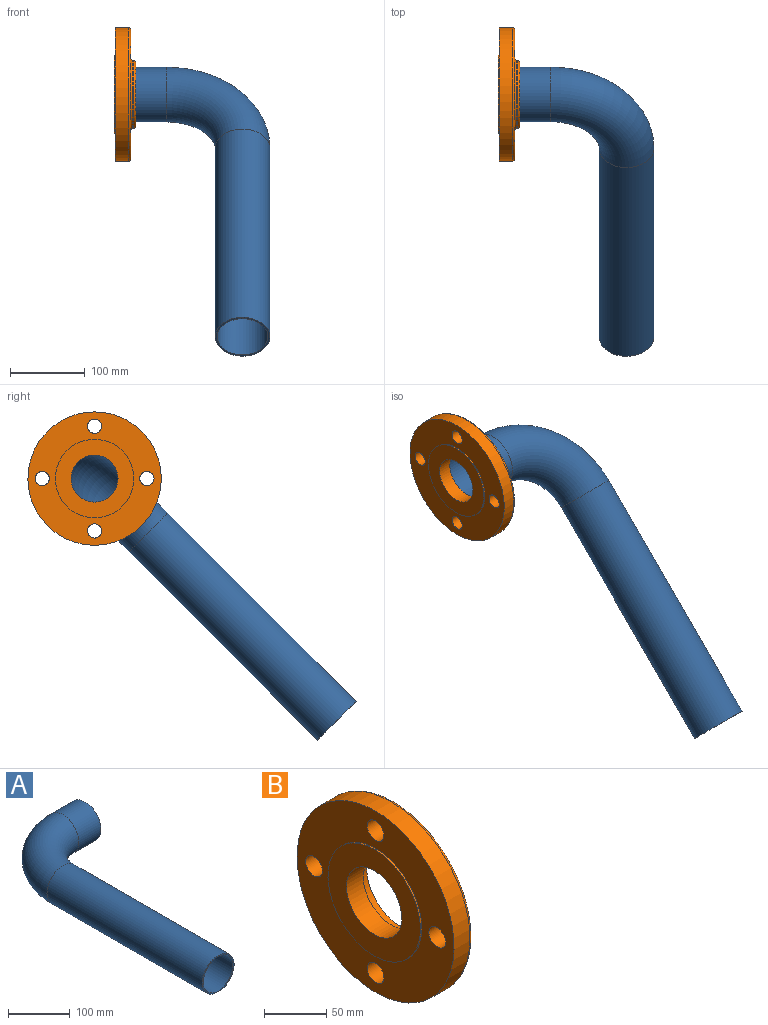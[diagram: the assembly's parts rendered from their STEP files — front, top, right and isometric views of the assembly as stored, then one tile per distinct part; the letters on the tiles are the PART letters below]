
ASSEMBLY  parts=2 mates=1
PART A: 8 faces, bbox 200.3x505.1x73 mm
  f0: plane 73.03x73.03mm, normal (0,-1,0), area 562.4mm2, adj f2,f5
  f1: plane 73.03x73.03mm, normal (1,0,0), area 562.4mm2, adj f4,f7
  f2: cylinder r=36.51mm len=355.6mm, axis (0,1,0), area 81579.9mm2, adj f0,f3
  f3: torus R=101.6mm, axis (0,0,-1), area 36613mm2, adj f2,f4
  f4: cylinder r=36.51mm len=73.03mm, axis (1,0,0), area 11654.3mm2, adj f1,f3
  f5: cylinder r=33.97mm len=355.6mm, axis (0,1,0), area 75904.8mm2, adj f0,f6
  f6: torus R=101.6mm, axis (0,0,-1), area 34066mm2, adj f5,f7
  f7: cylinder r=33.97mm len=67.95mm, axis (1,0,0), area 10843.5mm2, adj f1,f6
PART B: 17 faces, bbox 29x192.7x192.7 mm
  f0: cylinder r=89mm len=178mm, axis (-1,0,0), area 10055.2mm2, adj f1,f8
  f1: torus R=86.28mm, axis (-1,0,0), area 2361.6mm2, adj f0,f2
  f2: plane 172.56x172.56mm, normal (1,0,0), area 15099.7mm2, adj f1,f3,f10,f11,f12,f13
  f3: torus R=47.72mm, axis (-1,0,0), area 1234mm2, adj f2,f4
  f4: cylinder r=45mm len=90mm, axis (-1,0,0), area 357mm2, adj f3,f5
  f5: torus R=42.28mm, axis (-1,0,0), area 1180.9mm2, adj f4,f6
  f6: plane 84.56x84.56mm, normal (1,0,0), area 1233.7mm2, adj f5,f15
  f7: cylinder r=52.4mm len=104.8mm, axis (-1,0,0), area 526.8mm2, adj f8,f9
  f8: plane 178x178mm, normal (-1,0,0), area 15124.4mm2, adj f0,f7,f10,f11,f12,f13
  f9: plane 104.8x104.8mm, normal (-1,0,0), area 5538.4mm2, adj f7,f16
  f10: cylinder r=9.5mm len=20.7mm, axis (1,0,0), area 1235.6mm2, adj f2,f8
  f11: cylinder r=9.5mm len=20.7mm, axis (1,0,0), area 1235.6mm2, adj f2,f8
  f12: cylinder r=9.5mm len=20.7mm, axis (1,0,0), area 1235.6mm2, adj f2,f8
  f13: cylinder r=9.5mm len=20.7mm, axis (1,0,0), area 1235.6mm2, adj f2,f8
  f14: plane 74.7x74.7mm, normal (1,0,0), area 1295mm2, adj f15,f16
  f15: cylinder r=37.35mm len=74.7mm, axis (1,0,0), area 2346.8mm2, adj f6,f14
  f16: cylinder r=31.35mm len=62.7mm, axis (1,0,0), area 3742.6mm2, adj f9,f14
PLACE A rot(axis=(0,0.92,0.38),180deg) t=(-3137.98,-206.44,-206.44)mm fixed
PLACE B t=(-11,0,0)mm
MATE fastened A.f4 <-> B.f0  axis (-1,0,0) through (8,0,0)mm
